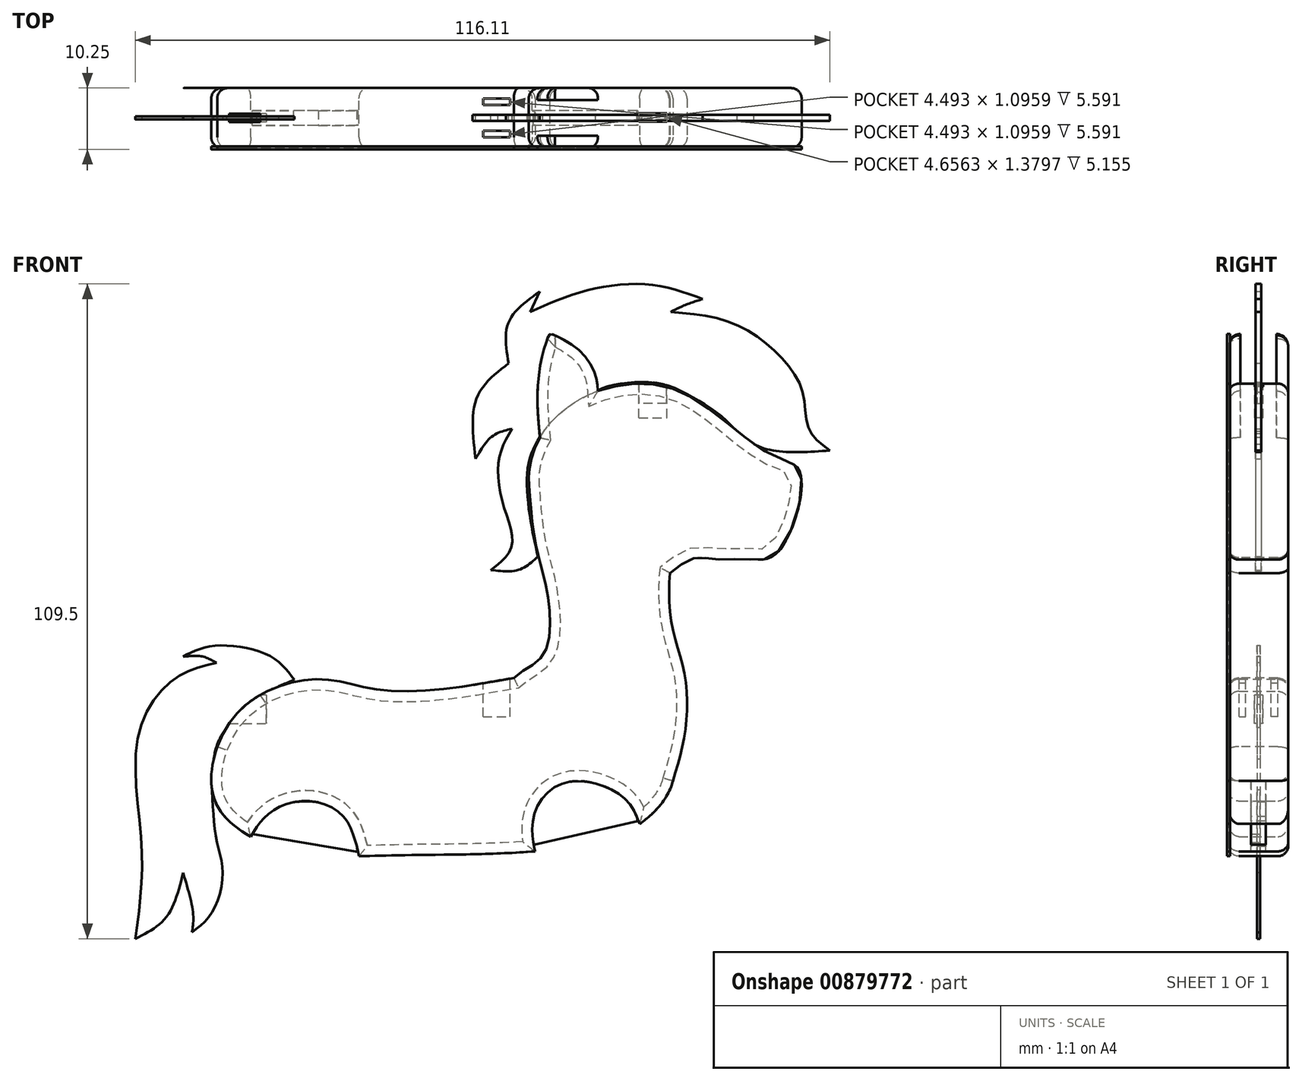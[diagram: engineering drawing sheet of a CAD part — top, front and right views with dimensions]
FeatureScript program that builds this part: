
annotation { "Feature Type Name" : "Feature", "Feature Type Description" : "" }
export const myFeature = defineFeature(function(context is Context, id is Id, definition is map)
    precondition{}
    {
        {
            var Q0;
            Q0=qCreatedBy(makeId("Front.planeOp"),FACE);
            var sketch = newSketch(context, id + "F0", { "sketchPlane" : qUnion([Q0])});
            skFitSpline(sketch, "E0", {"points": [v(-33.2, 0) * mm, v(-28.54, 6.87) * mm, v(-21.32, 10.6) * mm, v(-13.63, 11.07) * mm, v(-5.7, 9.44) * mm, v(9.9, 10.37) * mm, v(24.18, 12.18) * mm, v(36.67, 8.97) * mm, v(41.49, 3.61) * mm, v(42.74, 0) * mm], "startDerivative": vector(33.01, 85.06) * mm, "endDerivative": vector(14.23, -54.45) * mm});
            skFitSpline(sketch, "E1", {"points": [v(-33.2, 0) * mm, v(-33.2, -9.9) * mm, v(-23.18, -16.9) * mm, v(-11.45, -18.35) * mm, v(-2.59, -18.16) * mm, v(18.47, -17.62) * mm, v(36.5, -13.52) * mm, v(42.91, -6.02) * mm, v(42.74, 0) * mm], "startDerivative": vector(-29.89, -89.59) * mm, "endDerivative": vector(-13.7, 71.66) * mm});
            skSolve(sketch);
        }
        {
            var Q0;
            Q0=makeQuery(id+"F0.imprint","IMPRINT",FACE,{"disambiguationData":[TD([[makeQuery(id+"F0.imprint","IMPRINT",EDGE,{"derivedFrom":sQuery(id+"F0.wireOp",EDGE,"E0")}),-1.0]])]});
            extrude(context, id + "F1", {"entities" : qUnion([Q0]), "endBound" : BoundingType.SYMMETRIC, "oppositeDirection" : true, "depth" : 10 * mm, "offsetDistance" : 25.4 * mm});
        }
        {
            var Q0;
            Q0=makeQuery(id+"F1.opExtrude","CAP_FACE",FACE,{"disambiguationData":[OSD([sQuery(id+"F0.wireOp",EDGE,"E0"),sQuery(id+"F0.wireOp",EDGE,"E1")])],"isStart":false});
            cPlane(context, id + "F2", {"entities" : qUnion([Q0]), "cplaneType" : CPlaneType.OFFSET, "offset" : 5 * mm, "oppositeDirection" : true, "width" : 150 * mm, "height" : 150 * mm});
        }
        {
            var Q0;
            Q0=makeQuery(id+"F1.opExtrude","CAP_FACE",FACE,{"disambiguationData":[OSD([sQuery(id+"F0.wireOp",EDGE,"E0"),sQuery(id+"F0.wireOp",EDGE,"E1")])],"isStart":true});
            var sketch = newSketch(context, id + "F3", { "sketchPlane" : qUnion([Q0])});
            skPoint(sketch, "E2.6.internal.orphan", {"position": v(42.74, 40.01) * mm});
            skFitSpline(sketch, "E3", {"points": [v(42.74, -6.56) * mm, v(44.95, 2.08) * mm, v(44.95, 11.92) * mm, v(42.74, 20.9) * mm, v(42.74, 30.95) * mm, v(44.52, 35.98) * mm, v(47.36, 39.27) * mm], "startDerivative": vector(14.61, 47.07) * mm, "endDerivative": vector(24.83, 24.84) * mm});
            skFitSpline(sketch, "E4", {"points": [v(16.38, 11.48) * mm, v(21.18, 15.16) * mm, v(22.35, 22.73) * mm, v(21.04, 29.87) * mm, v(19.87, 34.67) * mm, v(19, 42.53) * mm, v(19, 46.46) * mm, v(21.04, 52.14) * mm, v(26.28, 57.38) * mm, v(32.83, 60.15) * mm, v(41.42, 60.3) * mm, v(50.15, 55.63) * mm, v(59.76, 48.65) * mm, v(64.28, 45.73) * mm, v(60.5, 32.49) * mm, v(55.57, 31.34) * mm, v(49.98, 31.34) * mm, v(46.33, 31.47) * mm, v(42.49, 29.02) * mm], "startDerivative": vector(93.38, 86.42) * mm, "endDerivative": vector(-81, -60.4) * mm});
            skSolve(sketch);
        }
        {
            var Q0;
            {var subQ0=sQuery(id+"F3.wireOp",EDGE,"E4");Q0=makeQuery(id+"F3.imprint","IMPRINT",FACE,{"disambiguationData":[TD([[makeQuery(id+"F3.imprint","IMPRINT",EDGE,{"derivedFrom":subQ0}),-1.0]])]});}
            extrude(context, id + "F4", {"entities" : qUnion([Q0]), "operationType" : NewBodyOperationType.ADD, "oppositeDirection" : true, "depth" : 10 * mm, "offsetDistance" : 25 * mm});
        }
        {
            var Q0;
            Q0=qCreatedBy(id+"F2.planeOp",FACE);
            var sketch = newSketch(context, id + "F5", { "sketchPlane" : qUnion([Q0])});
            skFitSpline(sketch, "E5", {"points": [v(-37.5, -13.17) * mm, v(-35.34, -9.12) * mm, v(-30.24, -6.22) * mm, v(-24.14, -6.32) * mm, v(-20.04, -10.52) * mm, v(-19.54, -15.32) * mm, v(-19.94, -17.52) * mm], "startDerivative": vector(8.46, 26) * mm, "endDerivative": vector(-4, -17.16) * mm});
            skFitSpline(sketch, "E6", {"points": [v(-37.5, -13.17) * mm, v(-32.74, -15.42) * mm, v(-26.44, -17.02) * mm, v(-19.94, -17.52) * mm], "startDerivative": vector(13.82, -8.43) * mm, "endDerivative": vector(18.64, -0.82) * mm});
            skSolve(sketch);
        }
        {
            var Q0;
            Q0=makeQuery(id+"F5.imprint","IMPRINT",FACE,{"disambiguationData":[TD([[makeQuery(id+"F5.imprint","IMPRINT",EDGE,{"derivedFrom":sQuery(id+"F5.wireOp",EDGE,"E5")}),-1.0]])]});
            extrude(context, id + "F6", {"entities" : qUnion([Q0]), "operationType" : NewBodyOperationType.REMOVE, "endBound" : BoundingType.SYMMETRIC, "depth" : 25 * mm, "offsetDistance" : 25 * mm});
        }
        {
            var Q0;
            {var subQ0=sQuery(id+"F0.wireOp",EDGE,"E1");var subQ1=sQuery(id+"F0.wireOp",EDGE,"E0");Q0=makeQuery(id+"F4.boolean.opBoolean","MERGE",FACE,{"derivedFrom":[makeQuery(id+"F1.opExtrude","CAP_FACE",FACE,{"disambiguationData":[OSD([subQ1,subQ0])],"isStart":true}),makeQuery(id+"F4.opExtrude","CAP_FACE",FACE,{"disambiguationData":[OSD([subQ1,subQ0,sQuery(id+"F3.wireOp",EDGE,"E3"),sQuery(id+"F3.wireOp",EDGE,"E4")])],"isStart":true})]});}
            var sketch = newSketch(context, id + "F7", { "sketchPlane" : qUnion([Q0])});
            skFitSpline(sketch, "E7", {"points": [v(-27.6, -15.04) * mm, v(-25.8, -12.41) * mm, v(-22.73, -10.04) * mm, v(-17.2, -9.15) * mm, v(-12.25, -11.52) * mm, v(-10.27, -15.28) * mm, v(-9.49, -18.33) * mm], "startDerivative": vector(11.26, 18.56) * mm, "endDerivative": vector(4.63, -20.4) * mm});
            skFitSpline(sketch, "E8", {"points": [v(-27.6, -15.04) * mm, v(-23.72, -17.52) * mm, v(-19.17, -19.04) * mm, v(-13.14, -19.24) * mm, v(-9.49, -18.33) * mm], "startDerivative": vector(15.48, -10.85) * mm, "endDerivative": vector(15.05, 4.94) * mm});
            skSolve(sketch);
        }
        {
            var Q0;
            {var subQ0=sQuery(id+"F7.wireOp",EDGE,"E7");Q0=makeQuery(id+"F7.imprint","IMPRINT",FACE,{"disambiguationData":[TD([[makeQuery(id+"F7.imprint","IMPRINT",EDGE,{"derivedFrom":subQ0}),-1.0]])]});}
            var Q1;
            {var subQ0=sQuery(id+"F7.wireOp",EDGE,"E8");Q1=makeQuery(id+"F7.imprint","IMPRINT",FACE,{"disambiguationData":[TD([[makeQuery(id+"F7.imprint","IMPRINT",EDGE,{"derivedFrom":subQ0}),1.0]])]});}
            extrude(context, id + "F8", {"entities" : qUnion([Q0, Q1]), "operationType" : NewBodyOperationType.REMOVE, "endBound" : BoundingType.SYMMETRIC, "depth" : 25 * mm, "offsetDistance" : 25 * mm});
        }
        {
            var Q0;
            Q0=qCreatedBy(id+"F2.planeOp",FACE);
            var sketch = newSketch(context, id + "F9", { "sketchPlane" : qUnion([Q0])});
            skLineSegment(sketch, "E9", {"start": v(-37.11, -12.48) * mm, "end": v(-19.8, -16.38) * mm});
            skFitSpline(sketch, "E10", {"points": [v(-37.11, -12.48) * mm, v(-35.65, -8.5) * mm, v(-31.83, -6.07) * mm, v(-27.77, -5.17) * mm, v(-23.7, -5.74) * mm, v(-21.27, -7.69) * mm, v(-19.4, -10.29) * mm, v(-18.75, -13.38) * mm, v(-19.8, -16.38) * mm], "startDerivative": vector(6.68, 32.27) * mm, "endDerivative": vector(-12.35, -25.4) * mm});
            skSolve(sketch);
        }
        {
            var Q0;
            Q0 = qSketchRegion(id + "F9", true);
            extrude(context, id + "F10", {"entities" : qUnion([Q0]), "operationType" : NewBodyOperationType.ADD, "endBound" : BoundingType.SYMMETRIC, "depth" : 2.5 * mm, "offsetDistance" : 25 * mm});
        }
        {
            var Q0;
            Q0=qCreatedBy(id+"F2.planeOp",FACE);
            var sketch = newSketch(context, id + "F11", { "sketchPlane" : qUnion([Q0])});
            skLineSegment(sketch, "E11", {"start": v(9.73, -17.6) * mm, "end": v(27.36, -14.63) * mm});
            skFitSpline(sketch, "E12", {"points": [v(9.73, -17.6) * mm, v(10.49, -14.3) * mm, v(12.65, -11.06) * mm, v(15.9, -9.39) * mm, v(21.25, -9.44) * mm, v(24.93, -11.28) * mm, v(27.36, -14.63) * mm], "startDerivative": vector(3.2, 21.67) * mm, "endDerivative": vector(13, -21.78) * mm});
            skSolve(sketch);
        }
        {
            var Q0;
            Q0=makeQuery(id+"F11.imprint","IMPRINT",FACE,{"disambiguationData":[TD([[makeQuery(id+"F11.imprint","IMPRINT",EDGE,{"derivedFrom":sQuery(id+"F11.wireOp",EDGE,"E11")}),1.0]])]});
            extrude(context, id + "F12", {"entities" : qUnion([Q0]), "operationType" : NewBodyOperationType.ADD, "endBound" : BoundingType.SYMMETRIC, "depth" : 2.5 * mm, "offsetDistance" : 25 * mm});
        }
        {
            var Q0;
            {var subQ0=sQuery(id+"F0.wireOp",EDGE,"E1");var subQ1=sQuery(id+"F0.wireOp",EDGE,"E0");Q0=makeQuery(id+"F4.boolean.opBoolean","MERGE",FACE,{"derivedFrom":[makeQuery(id+"F1.opExtrude","CAP_FACE",FACE,{"disambiguationData":[OSD([subQ1,subQ0])],"isStart":true}),makeQuery(id+"F4.opExtrude","CAP_FACE",FACE,{"disambiguationData":[OSD([subQ1,subQ0,sQuery(id+"F3.wireOp",EDGE,"E3"),sQuery(id+"F3.wireOp",EDGE,"E4")])],"isStart":true})]});}
            var sketch = newSketch(context, id + "F13", { "sketchPlane" : qUnion([Q0])});
            skFitSpline(sketch, "E13", {"points": [v(30.45, 59.46) * mm, v(29.96, 62.3) * mm, v(27.26, 66.32) * mm, v(23.46, 68.67) * mm, v(22.42, 68.95) * mm, v(22, 68.19) * mm, v(21.1, 65.21) * mm, v(20.34, 58.92) * mm, v(20.76, 51.66) * mm], "startDerivative": vector(-1.8, 24.1) * mm, "endDerivative": vector(3.93, -40.33) * mm});
            skSolve(sketch);
        }
        {
            var Q0;
            Q0 = qSketchRegion(id + "F13", true);
            var Q1;
            {var subQ0=sQuery(id+"F13.wireOp",EDGE,"E13");Q1=makeQuery(id+"F13.imprint","IMPRINT",FACE,{"disambiguationData":[TD([[makeQuery(id+"F13.imprint","IMPRINT",EDGE,{"derivedFrom":subQ0}),1.0]])]});}
            extrude(context, id + "F14", {"entities" : qUnion([Q0, Q1]), "oppositeDirection" : true, "depth" : 2 * mm, "offsetDistance" : 25 * mm});
        }
        {
            var Q0;
            Q0=makeQuery(id+"F14.opExtrude","SWEPT_BODY",BODY,{"disambiguationData":[OSD([sQuery(id+"F3.wireOp",EDGE,"E4"),sQuery(id+"F13.wireOp",EDGE,"E13")])]});
            var Q1;
            Q1=qCreatedBy(makeId("Front.planeOp"),FACE);
            mirror(context, id + "F15", {"operationType" : NewBodyOperationType.ADD, "entities" : qUnion([Q0]), "mirrorPlane" : qUnion([Q1])});
        }
        {
            var Q0;
            Q0=qCreatedBy(makeId("Top.planeOp"),FACE);
            cPlane(context, id + "F16", {"entities" : qUnion([Q0]), "cplaneType" : CPlaneType.OFFSET, "offset" : 15 * mm, "width" : 150 * mm, "height" : 150 * mm});
        }
        {
            var Q0;
            Q0=qCreatedBy(id+"F16.planeOp",FACE);
            var sketch = newSketch(context, id + "F17", { "sketchPlane" : qUnion([Q0])});
            skLineSegment(sketch, "E14.bottom", {"start": v(11.25, 3.24) * mm, "end": v(15.74, 3.24) * mm});
            skLineSegment(sketch, "E14.top", {"start": v(11.25, 2.14) * mm, "end": v(15.74, 2.14) * mm});
            skLineSegment(sketch, "E14.left", {"start": v(11.25, 3.24) * mm, "end": v(11.25, 2.14) * mm});
            skLineSegment(sketch, "E14.right", {"start": v(15.74, 3.24) * mm, "end": v(15.74, 2.14) * mm});
            skLineSegment(sketch, "E15.MirrorCS", {"start": v(11.25, -3.24) * mm, "end": v(15.74, -3.24) * mm});
            skLineSegment(sketch, "E16.MirrorCS", {"start": v(11.25, -2.14) * mm, "end": v(15.74, -2.14) * mm});
            skLineSegment(sketch, "E17.MirrorCS", {"start": v(15.74, -3.24) * mm, "end": v(15.74, -2.14) * mm});
            skLineSegment(sketch, "E18.MirrorCS", {"start": v(11.25, -3.24) * mm, "end": v(11.25, -2.14) * mm});
            skSolve(sketch);
        }
        {
            var Q0;
            Q0=makeQuery(id+"F17.imprint","IMPRINT",FACE,{"disambiguationData":[TD([[makeQuery(id+"F17.imprint","IMPRINT",EDGE,{"derivedFrom":sQuery(id+"F17.wireOp",EDGE,"E14.bottom")}),-1.0]])]});
            var Q1;
            Q1=makeQuery(id+"F17.imprint","IMPRINT",FACE,{"disambiguationData":[TD([[makeQuery(id+"F17.imprint","IMPRINT",EDGE,{"derivedFrom":sQuery(id+"F17.wireOp",EDGE,"E15.MirrorCS")}),1.0]])]});
            extrude(context, id + "F18", {"entities" : qUnion([Q0, Q1]), "operationType" : NewBodyOperationType.REMOVE, "oppositeDirection" : true, "depth" : 10 * mm, "offsetDistance" : 25 * mm});
        }
        {
            var Q0;
            Q0=qCreatedBy(makeId("Top.planeOp"),FACE);
            cPlane(context, id + "F19", {"entities" : qUnion([Q0]), "cplaneType" : CPlaneType.OFFSET, "offset" : 65 * mm, "width" : 150 * mm, "height" : 150 * mm});
        }
        {
            var Q0;
            Q0=qCreatedBy(id+"F19.planeOp",FACE);
            var sketch = newSketch(context, id + "F20", { "sketchPlane" : qUnion([Q0])});
            skLineSegment(sketch, "E19.bottom", {"start": v(37.3, 0.77) * mm, "end": v(41.96, 0.77) * mm});
            skLineSegment(sketch, "E19.top", {"start": v(37.3, -0.61) * mm, "end": v(41.96, -0.61) * mm});
            skLineSegment(sketch, "E19.left", {"start": v(37.3, 0.77) * mm, "end": v(37.3, -0.61) * mm});
            skLineSegment(sketch, "E19.right", {"start": v(41.96, 0.77) * mm, "end": v(41.96, -0.61) * mm});
            skSolve(sketch);
        }
        {
            var Q0;
            Q0=makeQuery(id+"F20.imprint","IMPRINT",FACE,{"disambiguationData":[TD([[makeQuery(id+"F20.imprint","IMPRINT",EDGE,{"derivedFrom":sQuery(id+"F20.wireOp",EDGE,"E19.bottom")}),-1.0]])]});
            extrude(context, id + "F21", {"entities" : qUnion([Q0]), "operationType" : NewBodyOperationType.REMOVE, "oppositeDirection" : true, "depth" : 10 * mm, "offsetDistance" : 25 * mm});
        }
        {
            var Q0;
            Q0=qCreatedBy(makeId("Right.planeOp"),FACE);
            cPlane(context, id + "F22", {"entities" : qUnion([Q0]), "cplaneType" : CPlaneType.OFFSET, "offset" : 35 * mm, "oppositeDirection" : true, "width" : 150 * mm, "height" : 150 * mm});
        }
        {
            var Q0;
            Q0=qCreatedBy(id+"F22.planeOp",FACE);
            var sketch = newSketch(context, id + "F23", { "sketchPlane" : qUnion([Q0])});
            skLineSegment(sketch, "E20.bottom", {"start": v(0.73, 8.63) * mm, "end": v(-0.68, 8.63) * mm});
            skLineSegment(sketch, "E20.top", {"start": v(0.73, 3.89) * mm, "end": v(-0.68, 3.89) * mm});
            skLineSegment(sketch, "E20.left", {"start": v(0.73, 8.63) * mm, "end": v(0.73, 3.89) * mm});
            skLineSegment(sketch, "E20.right", {"start": v(-0.68, 8.63) * mm, "end": v(-0.68, 3.89) * mm});
            skSolve(sketch);
        }
        {
            var Q0;
            Q0=makeQuery(id+"F23.imprint","IMPRINT",FACE,{"disambiguationData":[TD([[makeQuery(id+"F23.imprint","IMPRINT",EDGE,{"derivedFrom":sQuery(id+"F23.wireOp",EDGE,"E20.bottom")}),1.0]])]});
            extrude(context, id + "F24", {"entities" : qUnion([Q0]), "operationType" : NewBodyOperationType.REMOVE, "depth" : 10 * mm, "offsetDistance" : 25 * mm});
        }
        {
            var Q0;
            {var subQ0=sQuery(id+"F3.wireOp",EDGE,"E4");var subQ1=sQuery(id+"F0.wireOp",EDGE,"E1");var subQ2=sQuery(id+"F0.wireOp",EDGE,"E0");Q0=makeQuery(id+"F15.boolean.opBoolean","MERGE",FACE,{"derivedFrom":[makeQuery(id+"F4.boolean.opBoolean","MERGE",FACE,{"derivedFrom":[makeQuery(id+"F1.opExtrude","CAP_FACE",FACE,{"disambiguationData":[OSD([subQ2,subQ1])],"isStart":true}),makeQuery(id+"F4.opExtrude","CAP_FACE",FACE,{"disambiguationData":[OSD([subQ2,subQ1,sQuery(id+"F3.wireOp",EDGE,"E3"),subQ0])],"isStart":true})]}),makeQuery(id+"F14.opExtrude","CAP_FACE",FACE,{"disambiguationData":[OSD([subQ0,sQuery(id+"F13.wireOp",EDGE,"E13")])],"isStart":true})]});}
            var sketch = newSketch(context, id + "F25", { "sketchPlane" : qUnion([Q0])});
            skSolve(sketch);
        }
        {
            var Q0;
            {var subQ0=sQuery(id+"F3.wireOp",EDGE,"E4");var subQ1=sQuery(id+"F0.wireOp",EDGE,"E1");var subQ2=sQuery(id+"F0.wireOp",EDGE,"E0");Q0=makeQuery(id+"F15.boolean.opBoolean","MERGE",FACE,{"derivedFrom":[makeQuery(id+"F4.boolean.opBoolean","MERGE",FACE,{"derivedFrom":[makeQuery(id+"F1.opExtrude","CAP_FACE",FACE,{"disambiguationData":[OSD([subQ2,subQ1])],"isStart":true}),makeQuery(id+"F4.opExtrude","CAP_FACE",FACE,{"disambiguationData":[OSD([subQ2,subQ1,sQuery(id+"F3.wireOp",EDGE,"E3"),subQ0])],"isStart":true})]}),makeQuery(id+"F14.opExtrude","CAP_FACE",FACE,{"disambiguationData":[OSD([subQ0,sQuery(id+"F13.wireOp",EDGE,"E13")])],"isStart":true})]});}
            var Q1;
            {var subQ0=sQuery(id+"F3.wireOp",EDGE,"E4");var subQ1=sQuery(id+"F0.wireOp",EDGE,"E1");var subQ2=sQuery(id+"F0.wireOp",EDGE,"E0");Q1=makeQuery(id+"F15.boolean.opBoolean","MERGE",FACE,{"derivedFrom":[makeQuery(id+"F4.boolean.opBoolean","MERGE",FACE,{"derivedFrom":[makeQuery(id+"F1.opExtrude","CAP_FACE",FACE,{"disambiguationData":[OSD([subQ2,subQ1])],"isStart":false}),makeQuery(id+"F4.opExtrude","CAP_FACE",FACE,{"disambiguationData":[OSD([subQ2,subQ1,sQuery(id+"F3.wireOp",EDGE,"E3"),subQ0])],"isStart":false})]}),makeQuery(id+"F15.opPattern","COPY",FACE,{"derivedFrom":makeQuery(id+"F14.opExtrude","CAP_FACE",FACE,{"disambiguationData":[OSD([subQ0,sQuery(id+"F13.wireOp",EDGE,"E13")])],"isStart":true}),"instanceName":"1"})]});}
            fillet(context, id + "F26", {"entities" : qUnion([Q0, Q1]), "radius" : 1.75 * mm, "tangentPropagation" : true, "allowEdgeOverflow" : false});
        }
        {
            var Q0;
            Q0=qCreatedBy(makeId("Front.planeOp"),FACE);
            var sketch = newSketch(context, id + "F27", { "sketchPlane" : qUnion([Q0])});
            skFitSpline(sketch, "E21", {"points": [v(15.52, 64.1) * mm, v(10.2, 58.35) * mm, v(10, 48.15) * mm], "startDerivative": vector(-13.95, -10.7) * mm, "endDerivative": vector(2.53, -20.97) * mm});
            skFitSpline(sketch, "E22", {"points": [v(10, 48.15) * mm, v(12.76, 51.87) * mm, v(16.06, 53.14) * mm], "startDerivative": vector(4.67, 8.1) * mm, "endDerivative": vector(7.51, 1.75) * mm});
            skFitSpline(sketch, "E23", {"points": [v(16.06, 53.14) * mm, v(13.93, 48.15) * mm, v(14.67, 40.28) * mm, v(16.06, 33.58) * mm, v(12.55, 29.54) * mm], "startDerivative": vector(-11.54, -19.96) * mm, "endDerivative": vector(-20.42, -15.8) * mm});
            skFitSpline(sketch, "E24", {"points": [v(12.55, 29.54) * mm, v(17.12, 29.54) * mm, v(20.42, 31.77) * mm], "startDerivative": vector(9.36, -1.2) * mm, "endDerivative": vector(6.34, 5.74) * mm});
            skFitSpline(sketch, "E25", {"points": [v(20.73, 51.76) * mm, v(19.03, 48.15) * mm, v(18.6, 42.83) * mm, v(19.46, 36.34) * mm, v(20.42, 31.77) * mm], "startDerivative": vector(-8.9, -15.41) * mm, "endDerivative": vector(4.03, -18.09) * mm});
            skFitSpline(sketch, "E26", {"points": [v(20.73, 51.76) * mm, v(23.71, 55.06) * mm, v(28.5, 58.14) * mm, v(30.94, 59.84) * mm, v(36.04, 60.9) * mm, v(41.78, 60.48) * mm, v(47, 58.03) * mm, v(51.78, 54.63) * mm, v(57.41, 50.17) * mm, v(69.21, 49.53) * mm], "startDerivative": vector(26.25, 35.31) * mm, "endDerivative": vector(83.37, 6) * mm});
            skFitSpline(sketch, "E27", {"points": [v(69.21, 49.53) * mm, v(65.7, 53.14) * mm, v(64.75, 59.1) * mm, v(60.6, 65.58) * mm, v(52.73, 70.9) * mm, v(42.63, 72.7) * mm], "startDerivative": vector(-26.4, 19.3) * mm, "endDerivative": vector(-44.94, 3.95) * mm});
            skFitSpline(sketch, "E28", {"points": [v(15.52, 64.1) * mm, v(15.52, 70.98) * mm, v(20.73, 76.1) * mm], "startDerivative": vector(-2.53, 14.94) * mm, "endDerivative": vector(12.87, 9.12) * mm});
            skFitSpline(sketch, "E29", {"points": [v(20.73, 76.1) * mm, v(19.16, 72.7) * mm], "startDerivative": vector(-1.57, -3.4) * mm, "endDerivative": vector(-1.57, -3.4) * mm});
            skFitSpline(sketch, "E30", {"points": [v(19.16, 72.7) * mm, v(27.98, 76.1) * mm, v(39.13, 77.28) * mm, v(47.95, 74.85) * mm], "startDerivative": vector(25.7, 11.57) * mm, "endDerivative": vector(26.25, -9.89) * mm});
            skFitSpline(sketch, "E31", {"points": [v(42.63, 72.7) * mm, v(45.07, 73.86) * mm, v(47.95, 74.85) * mm], "startDerivative": vector(4.9, 2.5) * mm, "endDerivative": vector(5.73, 1.8) * mm});
            skSolve(sketch);
        }
        {
            var Q0;
            Q0=qCreatedBy(id+"F2.planeOp",FACE);
            var sketch = newSketch(context, id + "F28", { "sketchPlane" : qUnion([Q0])});
            skLineSegment(sketch, "E32", {"start": v(-41.87, 60.4) * mm, "end": v(-41.87, 57.38) * mm});
            skLineSegment(sketch, "E33", {"start": v(-41.87, 57.38) * mm, "end": v(-37.12, 57.38) * mm});
            skLineSegment(sketch, "E34", {"start": v(-37.12, 57.38) * mm, "end": v(-37.12, 60.79) * mm});
            skFitSpline(sketch, "E35", {"points": [v(-41.87, 60.4) * mm, v(-39.61, 61.19) * mm, v(-37.12, 60.79) * mm], "startDerivative": vector(4.5, 2.2) * mm, "endDerivative": vector(5.01, -1.39) * mm});
            skSolve(sketch);
        }
        {
            var Q0;
            Q0=makeQuery(id+"F28.imprint","IMPRINT",FACE,{"disambiguationData":[TD([[makeQuery(id+"F28.imprint","IMPRINT",EDGE,{"derivedFrom":sQuery(id+"F28.wireOp",EDGE,"E32")}),1.0]])]});
            extrude(context, id + "F29", {"entities" : qUnion([Q0]), "endBound" : BoundingType.SYMMETRIC, "depth" : .5 * mm, "offsetDistance" : 25 * mm});
        }
        {
            var Q0;
            Q0=makeQuery(id+"F27.imprint","IMPRINT",FACE,{"disambiguationData":[TD([[makeQuery(id+"F27.imprint","IMPRINT",EDGE,{"derivedFrom":sQuery(id+"F27.wireOp",EDGE,"E21")}),1.0]])]});
            extrude(context, id + "F30", {"entities" : qUnion([Q0]), "operationType" : NewBodyOperationType.ADD, "endBound" : BoundingType.SYMMETRIC, "depth" : 1 * mm, "offsetDistance" : 25 * mm});
        }
        {
            var Q0;
            Q0=qCreatedBy(id+"F2.planeOp",FACE);
            var sketch = newSketch(context, id + "F31", { "sketchPlane" : qUnion([Q0])});
            skFitSpline(sketch, "E36", {"points": [v(20.32, 11.17) * mm, v(24.42, 15.16) * mm, v(33.66, 16.84) * mm, v(38.92, 15.06) * mm], "startDerivative": vector(10.55, 14.44) * mm, "endDerivative": vector(15.3, -7.75) * mm});
            skFitSpline(sketch, "E37", {"points": [v(38.92, 15.06) * mm, v(35.66, 15.06) * mm, v(33.35, 14) * mm], "startDerivative": vector(-6.45, 0.6) * mm, "endDerivative": vector(-4.65, -2.77) * mm});
            skFitSpline(sketch, "E38", {"points": [v(33.35, 14) * mm, v(39.97, 11.6) * mm, v(46.38, 1.92) * mm, v(45.85, -17.1) * mm, v(46.9, -32.12) * mm], "startDerivative": vector(36.05, -7.86) * mm, "endDerivative": vector(7.3, -52.52) * mm});
            skFitSpline(sketch, "E39", {"points": [v(46.9, -32.12) * mm, v(41.75, -28.55) * mm, v(38.92, -21.1) * mm], "startDerivative": vector(-12.28, 6.09) * mm, "endDerivative": vector(-3.86, 15.79) * mm});
            skFitSpline(sketch, "E40", {"points": [v(38.92, -21.1) * mm, v(37.24, -28.03) * mm, v(37.45, -31.07) * mm], "startDerivative": vector(-3.78, -12.61) * mm, "endDerivative": vector(1.19, -6.96) * mm});
            skFitSpline(sketch, "E41", {"points": [v(37.45, -31.07) * mm, v(34.07, -27.71) * mm, v(32.3, -21.1) * mm, v(33.35, -15.42) * mm, v(34.07, -7.22) * mm], "startDerivative": vector(-16.91, 12.88) * mm, "endDerivative": vector(1.35, 30.55) * mm});
            skFitSpline(sketch, "E42", {"points": [v(20.32, 11.17) * mm, v(24.52, 9.38) * mm, v(28.2, 7.18) * mm, v(31.04, 4.02) * mm, v(33.35, 0) * mm, v(34.07, -7.22) * mm], "startDerivative": vector(22.14, -8.94) * mm, "endDerivative": vector(0.55, -32.26) * mm});
            skSolve(sketch);
        }
        {
            var Q0;
            Q0=qCreatedBy(id+"F2.planeOp",FACE);
            var sketch = newSketch(context, id + "F32", { "sketchPlane" : qUnion([Q0])});
            skLineSegment(sketch, "E43", {"start": v(26, 8.57) * mm, "end": v(22.88, 3.88) * mm});
            skLineSegment(sketch, "E44", {"start": v(22.88, 3.88) * mm, "end": v(28.72, 0) * mm});
            skLineSegment(sketch, "E45", {"start": v(28.72, 0) * mm, "end": v(31.3, 3.88) * mm});
            skFitSpline(sketch, "E46", {"points": [v(26, 8.57) * mm, v(28.43, 7.29) * mm, v(30.26, 5.6) * mm, v(31.3, 3.88) * mm], "startDerivative": vector(7.08, -3.27) * mm, "endDerivative": vector(3.03, -5.7) * mm});
            skSolve(sketch);
        }
        {
            var Q0;
            Q0 = qSketchRegion(id + "F32", true);
            var Q1;
            {var subQ1=sQuery(id+"F3.wireOp",EDGE,"E3");Q1=makeQuery(id+"F25.imprint","IMPRINT",FACE,{"disambiguationData":[TD([[makeQuery(id+"F25.imprint","IMPRINT",EDGE,{"derivedFrom":makeQuery(id+"F4.opExtrude","CAP_EDGE",EDGE,{"disambiguationData":[OSD([subQ1])],"isStart":true})}),1.0]])]});}
            extrude(context, id + "F33", {"entities" : qUnion([Q0, Q1]), "endBound" : BoundingType.SYMMETRIC, "depth" : .5 * mm, "offsetDistance" : 25 * mm});
        }
        {
            var Q0;
            Q0=makeQuery(id+"F31.imprint","IMPRINT",FACE,{"disambiguationData":[TD([[makeQuery(id+"F31.imprint","IMPRINT",EDGE,{"derivedFrom":sQuery(id+"F31.wireOp",EDGE,"E36")}),-1.0]])]});
            extrude(context, id + "F34", {"entities" : qUnion([Q0]), "operationType" : NewBodyOperationType.ADD, "endBound" : BoundingType.SYMMETRIC, "depth" : .5 * mm, "offsetDistance" : 25 * mm});
        }
    });
